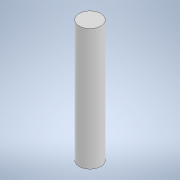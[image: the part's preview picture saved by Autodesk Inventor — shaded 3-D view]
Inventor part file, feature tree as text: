
AUTODESK INVENTOR PART (.ipt)
format: ipt  version: 2020 (Build 240168000, 168)  size: 90,112 bytes
history: native  units: mm
features: extrude x1, sketch x1
ambient origin geometry x8: Origin, YZ Plane, XZ Plane, XY Plane, X Axis, Y Axis, Z Axis, Center Point
bodies: Solid1 (feature_tree)
feature tree (2):
  extrude  "Extrusion1"  Depth=45.0mm TaperAngle=0.0deg
  sketch  "Sketch1"  dims[d0=8.0mm d1=45.0mm d2=0.0mm]
